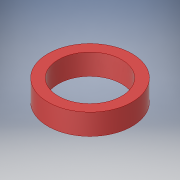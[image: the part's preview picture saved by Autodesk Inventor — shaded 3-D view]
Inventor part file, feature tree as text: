
AUTODESK INVENTOR PART (.ipt)
format: ipt  version: 2019 (Build 230136000, 136)  size: 100,864 bytes
history: native  units: in
note: dims shown in document units (in); Inventor stores cm internally (conversion verified against a paired STEP export)
features: extrude x1, sketch x1
ambient origin geometry x8: Origin, YZ Plane, XZ Plane, XY Plane, X Axis, Y Axis, Z Axis, Center Point
bodies: Solid1 (feature_tree)
feature tree (2):
  extrude  "Extrusion1"  Depth=0.125in
  sketch  "Sketch1"  dims[d0=0.377in d1=0.5in d2=0.125in d3=0.0in]
